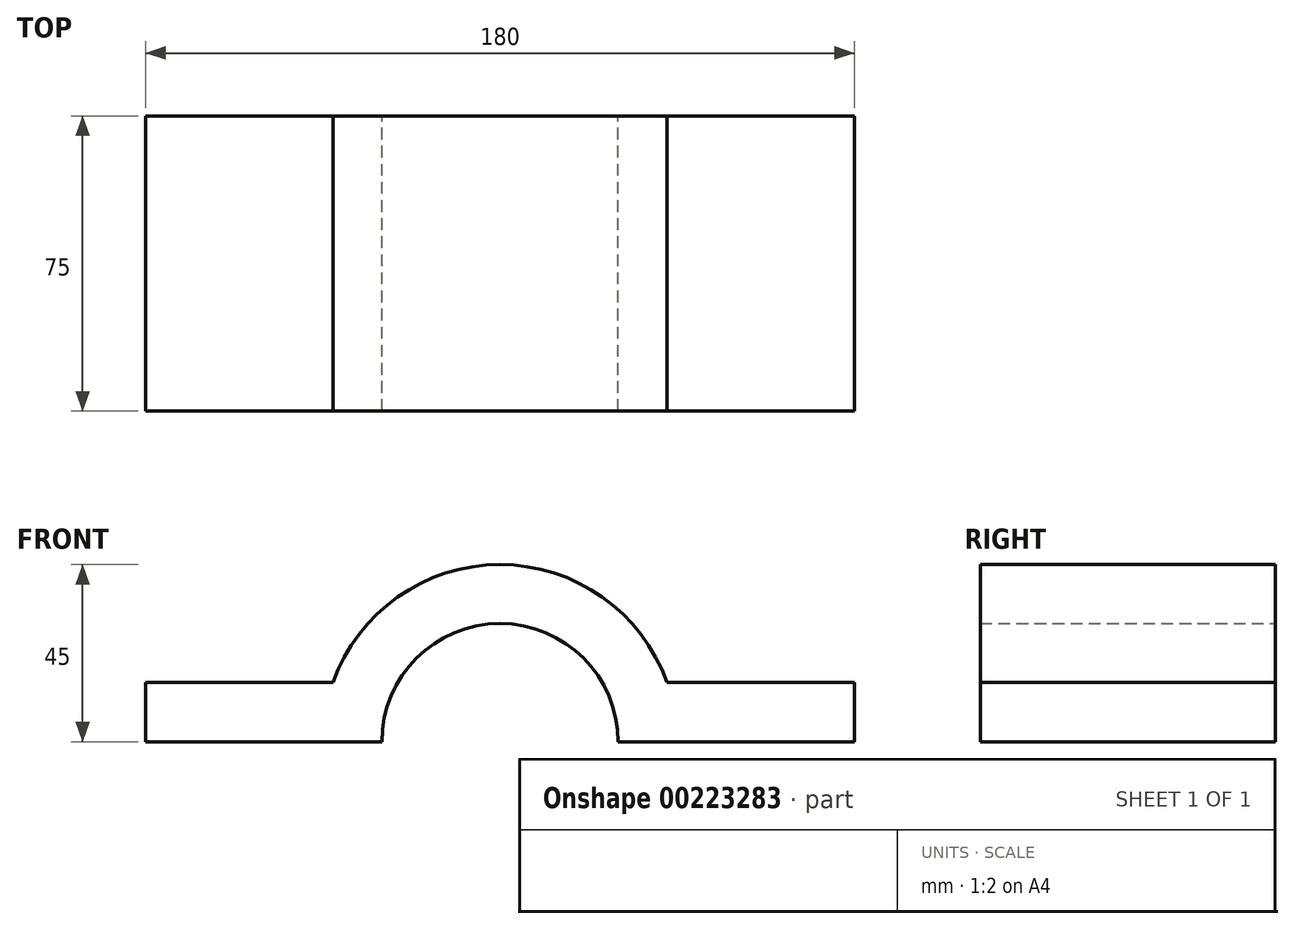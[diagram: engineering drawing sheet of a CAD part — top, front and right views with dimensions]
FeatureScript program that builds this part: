
annotation { "Feature Type Name" : "Feature", "Feature Type Description" : "" }
export const myFeature = defineFeature(function(context is Context, id is Id, definition is map)
    precondition{}
    {
        {
            var Q0;
            Q0=qCreatedBy(makeId("Front.planeOp"),FACE);
            var sketch = newSketch(context, id + "F0", { "sketchPlane" : qUnion([Q0])});
            skLineSegment(sketch, "E0", {"start": v(0, 0) * mm, "end": v(60, 0) * mm});
            skLineSegment(sketch, "E1", {"start": v(120, 0) * mm, "end": v(180, 0) * mm});
            skLineSegment(sketch, "E2", {"start": v(0, 15) * mm, "end": v(47.57, 15) * mm});
            skLineSegment(sketch, "E3", {"start": v(132.43, 15) * mm, "end": v(180, 15) * mm});
            skLineSegment(sketch, "E4", {"start": v(180, 15) * mm, "end": v(180, 0) * mm});
            skLineSegment(sketch, "E5", {"start": v(0, 15) * mm, "end": v(0, 0) * mm});
            skArc(sketch, "E6", {"start": v(132.43, 15) * mm, "mid": v(90, 45) * mm, "end": v(47.57, 15) * mm});
            skArc(sketch, "E7", {"start": v(120, 0) * mm, "mid": v(90, 30) * mm, "end": v(60, 0) * mm});
            skSolve(sketch);
        }
        {
            var Q0;
            Q0 = qSketchRegion(id + "F0", true);
            extrude(context, id + "F1", {"entities" : qUnion([Q0]), "depth" : 75 * mm});
        }
    });
